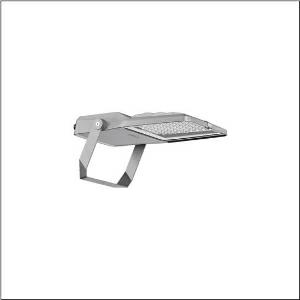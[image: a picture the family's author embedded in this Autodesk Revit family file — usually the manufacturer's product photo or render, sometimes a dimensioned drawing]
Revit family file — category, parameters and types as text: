
# Revit family: floodlight_fl_21_iq_mini___pl33t_5xa7772c5f1a_3dad
name_source: partatom
category: Lighting Fixtures
units: mm (PartAtom-declared; Revit-internal decimal feet)

## family parameters
Cut with Voids When Loaded = No
Host = Face
Light Source = No
Part Type = Normal
Room Calculation Point = No
Round Connector Dimension = Use Diameter
Shared = No

## types (1)
- --- (1 x LED, 11260 lm, 87.2 W, 4000K)
    Apparent Load = 87 VA
    CIE Flux Codes = 26 75 99 100 100
    Color Rendering = 80
    Color Temperature = 4000K
    Default Elevation = 1800 mm
    Description = Floodlight FL 21 iQ mini, floodlight, primary light control with lens, of PMMA, primary optical cover: protective disc, of toughened safety glass, transparent, light distribution: PL33T, light emission: direct distribution, installation type: surface-mounted, LED, High Power LED, rated luminous flux: 11.260lm, luminous efficacy: 129lm/W, light colour: 840, colour temperature: 4000K, control gear: iQ Street-Remote/DALI, control: Street-Remote, Auto-Match, Temp-Guard, Night-Set, Smart-Wire, Desk-Remote (wireless, voltage-free reading and setting of iQ features in the workshop via application-optimized NFC function/RFID function), optimised constant luminous flux control (CLO 2.0), with terminal, 6-pole, mains connection: 220..240V, AC, 50/60Hz, start of lifetime: 87W, end of service life: 92W, reduction: 40W, luminaire housing, of diecast aluminium, powder-coated, Siteco® metallic grey (DB 702S), corrosivity category C5 mid according to DIN EN ISO 12944, suitable for swimming pools, chlorine-resistant, sealing non-destructively replaceable, mounting bracket, of steel, galvanised, powder-coated, Siteco® metallic grey (DB 702S), protection rating (complete): IP66, insulation class (complete): insulation class II (safety insulation), certification: CE, ENEC, VDE, protection symbol: D, impact resistance: IK08, permissible operating ambient temperature: -40..+40°C, permissible operating ambient temperature for outdoor applications: -40..+50°C, standard: DIN EN 12944, LABS conformity tested according to VDMA 24364:2018-05, packaging unit: 1 piece

Light Distribution: PL33T
    Height = 70 mm
    Lamp = 1 x LED
    Lamp Light Flux = 11260 lm
    Lamp Power = 87.2 W
    Lamp count = 1
    Length = 485 mm
    Luminous efficacy = 129 lm/W
    Manufacturer = Siteco
    ModVariant = No
    Model = 5XA7772C5F1A
    Number of Poles = 1
    OnlyDefault = Yes
    Power Factor = 1
    Product Name = Floodlight FL 21 iQ mini | PL33T
    Product group = floodlight | pylon annexe
    ProductGroupID = 6200
    Protection Class = Protection class II
    Protection Degree = IP 66
    RLX_Detail_Level = 1
    RLX_Emergency_Light_Flux = 0 lm
    RLX_Emergency_Type = 0
    RLX_Emergency_Type_DB = No
    RlxData = <blob elided: 96289 chars, md5=ecfa6341>
    Socket = socket
    Standby Power = 0 W
    System Light Flux = 11260 lm
    System Power = 87 W
    Type Comments = factory setting: luminous flux: 100 % | dim-lin: 254 | 456 mA
    Type Image = l_1006845.jpg
    URL = http://relux.com
    VarID = @adj_149312
    Voltage = 0 V
    Weight = 0.00 kg
    Width = 337 mm

## geometry (parser evidence)
native form markers: Blend x4, Sweep x12
no freeform markers — native parametric forms only
